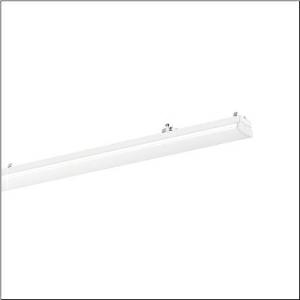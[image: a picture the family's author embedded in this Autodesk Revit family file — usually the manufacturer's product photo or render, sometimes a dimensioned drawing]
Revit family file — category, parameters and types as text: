
# Revit family: licross_21_recessed_opal_mo_52te1dmn46xg
name_source: partatom
category: Lighting Fixtures
units: mm (PartAtom-declared; Revit-internal decimal feet)

## family parameters
Cut with Voids When Loaded = No
Host = Face
Light Source = No
Part Type = Normal
Room Calculation Point = No
Round Connector Dimension = Use Diameter
Shared = No

## types (1)
- --- (1 x LED, 6270 lm, 35 W, 4000K)
    Apparent Load = 35 VA
    CIE Flux Codes = 44 73 91 87 100
    Color Rendering = 80
    Color Temperature = 4000K
    Default Elevation = 1800 mm
    Description = Licross 21 recessed opal MO, luminaire insert, of sheet steel, galvanised, coil coated, white, length: 1.500mm, width: 66mm, height: 67mm, LED rated luminous flux: 6.270lm, light colour: 840, SDCM (Standard Deviation of Colour Matching)MacAdam ≤ 3 SDCM (initial), control gear: ON/OFF Multilumen, with plug, 3-pole, with phase selection, mains connection: 220..240V, AC, 50/60Hz, rated input power: 35W, internal wiring halogen-free, primary optical cover: cover, of PMMA, light emission: direct with ceiling illumination distribution, primary light characteristic: symmetric, protection rating (complete): IP54, insulation class (complete): insulation class I (protective earthing), certification: CE, ENEC, VDE, UKCA, protection symbol: D if used in an environment with non-conductive dust loads with corresponding accessories, impact resistance: IK06, permissible ambient temperature for indoor applications: -35..+50°C, corresponds to IFS (International Featured Standards) requirements for safety and quality in the food industry, reducing of maximum allowable ambient temperature of 5°C with ceiling mounting, LABS conformity tested according to VDMA 24364:2018-05, The light source and the operating device comply with the requirements of the Ecodesign Regulation (EU) 2019/2020 and are replaceable in accordance with this regulation, packaging unit: 1 piece
    Height = 83 mm
    Lamp = 1 x LED
    Lamp Light Flux = 6270 lm
    Lamp Power = 35 W
    Lamp count = 1
    Length = 1500 mm
    Luminous efficacy = 179 lm/W
    Manufacturer = Siteco
    ModVariant = No
    Model = 52TE1DMN46XG
    Mounting Place = Ceiling
    Mounting Type = Pendant
    Number of Poles = 1
    OnlyDefault = Yes
    Power Factor = 1
    Product Name = Licross 21 recessed opal MO
    Product group = luminaire insert | ceiling pendant
    ProductGroupID = 901
    Protection Class = Protection class I
    Protection Degree = IP 54
    RLX_Detail_Level = 1
    RLX_Emergency_Light_Flux = 0 lm
    RLX_Emergency_Type = 0
    RLX_Emergency_Type_DB = No
    RlxData = <blob elided: 25089 chars, md5=5b943485>
    Socket = socket
    Standby Power = 0 W
    System Light Flux = 6270 lm
    System Power = 35 W
    Type Comments = factory setting: luminous flux: 100 % | (A | C | E) | 81 mA
    Type Image = l_1313666.jpg
    URL = http://relux.com
    VarID = @adj_027565
    Voltage = 0 V
    Weight = 0.00 kg
    Width = 76 mm

## geometry (parser evidence)
native form markers: Blend x4, Sweep x11
no freeform markers — native parametric forms only
